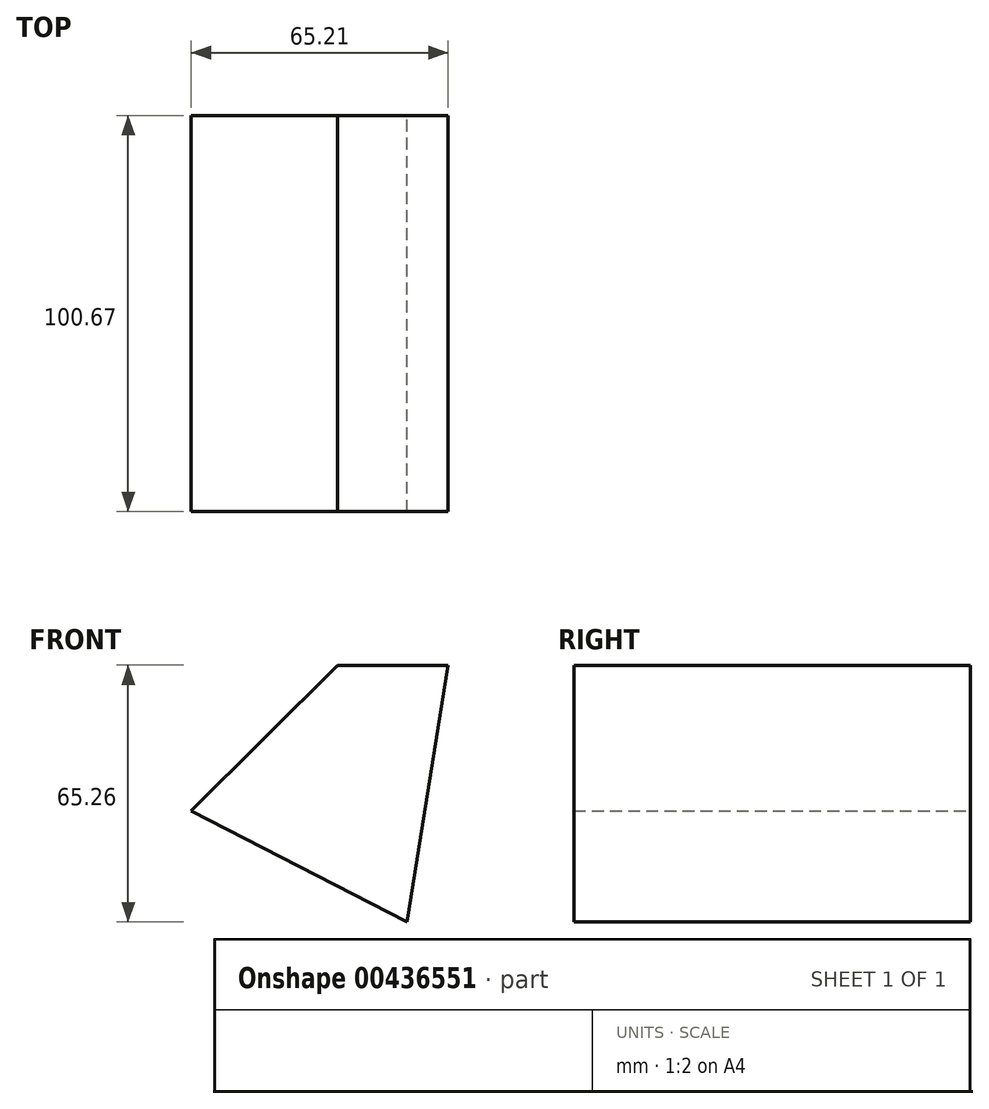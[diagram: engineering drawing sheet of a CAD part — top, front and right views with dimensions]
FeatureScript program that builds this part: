
annotation { "Feature Type Name" : "Feature", "Feature Type Description" : "" }
export const myFeature = defineFeature(function(context is Context, id is Id, definition is map)
    precondition{}
    {
        {
            var Q0;
            Q0=qCreatedBy(makeId("Front.planeOp"),FACE);
            var sketch = newSketch(context, id + "F0", { "sketchPlane" : qUnion([Q0])});
            skLineSegment(sketch, "E0", {"start": v(0, 0) * mm, "end": v(37.12, 36.97) * mm});
            skLineSegment(sketch, "E1", {"start": v(37.12, 36.97) * mm, "end": v(65.21, 36.97) * mm});
            skLineSegment(sketch, "E2", {"start": v(65.21, 36.97) * mm, "end": v(54.76, -28.29) * mm});
            skLineSegment(sketch, "E3", {"start": v(54.76, -28.29) * mm, "end": v(0, 0) * mm});
            skLineSegment(sketch, "E4", {"start": v(110.54, 129.53) * mm, "end": v(110.54, 93.45) * mm});
            skLineSegment(sketch, "E5", {"start": v(110.54, 93.45) * mm, "end": v(117.3, 93.45) * mm});
            skLineSegment(sketch, "E6", {"start": v(117.3, 93.45) * mm, "end": v(140.68, 125.51) * mm});
            skLineSegment(sketch, "E7", {"start": v(140.68, 125.51) * mm, "end": v(115.05, 133.29) * mm});
            skSolve(sketch);
        }
        {
            var Q0;
            Q0 = qSketchRegion(id + "F0", true);
            extrude(context, id + "F1", {"entities" : qUnion([Q0]), "depth" : 100.67 * mm});
        }
    });
